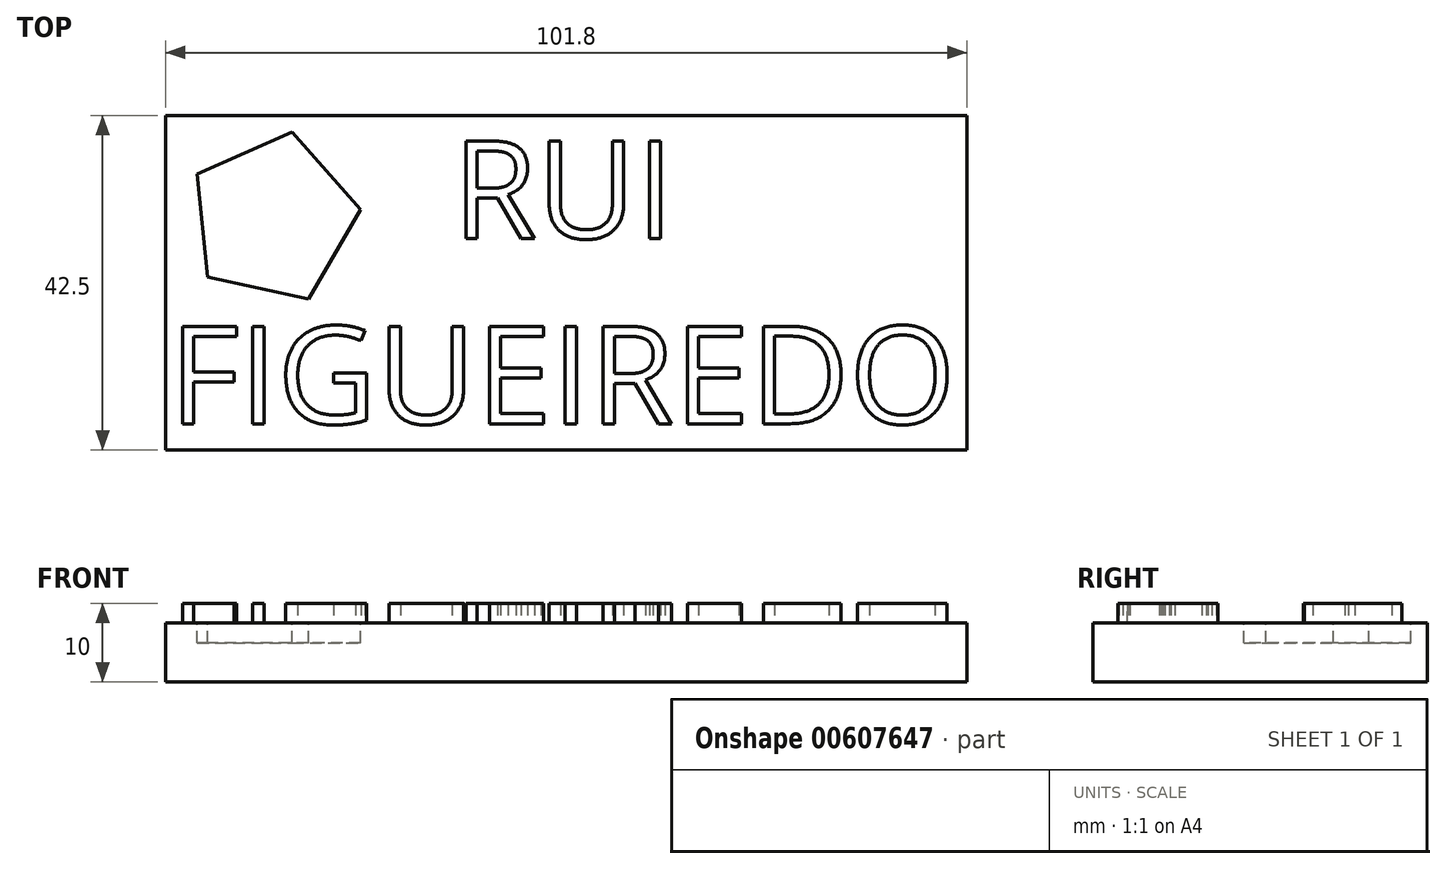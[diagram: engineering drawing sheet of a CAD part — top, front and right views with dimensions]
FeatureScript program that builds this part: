
annotation { "Feature Type Name" : "Feature", "Feature Type Description" : "" }
export const myFeature = defineFeature(function(context is Context, id is Id, definition is map)
    precondition{}
    {
        {
            var Q0;
            Q0=qCreatedBy(makeId("Top.planeOp"),FACE);
            var sketch = newSketch(context, id + "F0", { "sketchPlane" : qUnion([Q0])});
            skLineSegment(sketch, "E0.bottom", {"start": v(-49.13, 21.28) * mm, "end": v(52.67, 21.28) * mm});
            skLineSegment(sketch, "E0.top", {"start": v(-49.13, -21.22) * mm, "end": v(52.67, -21.22) * mm});
            skLineSegment(sketch, "E0.left", {"start": v(-49.13, 21.28) * mm, "end": v(-49.13, -21.22) * mm});
            skLineSegment(sketch, "E0.right", {"start": v(52.67, 21.28) * mm, "end": v(52.67, -21.22) * mm});
            skSolve(sketch);
        }
        {
            var Q0;
            Q0 = qSketchRegion(id + "F0", true);
            extrude(context, id + "F1", {"entities" : qUnion([Q0]), "depth" : 7.5 * mm, "offsetDistance" : 25 * mm});
        }
        {
            var Q0;
            Q0=makeQuery(id+"F1.opExtrude","CAP_FACE",FACE,{"disambiguationData":[OSD([sQuery(id+"F0.wireOp",EDGE,"E0.bottom"),sQuery(id+"F0.wireOp",EDGE,"E0.top"),sQuery(id+"F0.wireOp",EDGE,"E0.left"),sQuery(id+"F0.wireOp",EDGE,"E0.right")])],"isStart":false});
            var sketch = newSketch(context, id + "F2", { "sketchPlane" : qUnion([Q0])});
            skText(sketch, "E1", { "text": "        RUI\nFIGUEIREDO", "fontName": "OpenSans-Regular.ttf"});
            const initialGuessF2  = {"E1": [-0.04868, 0.00566, 1, 0, 0.01247]};
            skSetInitialGuess(sketch, initialGuessF2);
            skSolve(sketch);
        }
        {
            var Q0;
            {var subQ0=sQuery(id+"F0.wireOp",EDGE,"E0.top");var subQ1=sQuery(id+"F0.wireOp",EDGE,"E0.right");var subQ2=sQuery(id+"F0.wireOp",EDGE,"E0.bottom");var subQ3=sQuery(id+"F0.wireOp",EDGE,"E0.left");Q0=makeQuery(id+"FsaKldsH8CgI7bg_1.boolean.opBoolean","SPLIT",FACE,{"disambiguationData":[TD([makeQuery(id+"F1.opExtrude","SWEPT_FACE",FACE,{"disambiguationData":[OSD([subQ2])]})])],"derivedFrom":makeQuery(id+"F1.opExtrude","CAP_FACE",FACE,{"disambiguationData":[OSD([subQ2,subQ0,subQ3,subQ1])],"isStart":false})});}
            var sketch = newSketch(context, id + "F3", { "sketchPlane" : qUnion([Q0])});
            skCircle(sketch, "E2.cCircle", {"center": v(-35.46, 8.21) * mm, "radius": 9.05 * mm, "construction": true});
            skLineSegment(sketch, "E2.0", {"start": v(-24.32, 9.33) * mm, "end": v(-30.95, -2.03) * mm});
            skLineSegment(sketch, "E2.1", {"start": v(-30.95, -2.03) * mm, "end": v(-43.8, 0.76) * mm});
            skLineSegment(sketch, "E2.2", {"start": v(-43.8, 0.76) * mm, "end": v(-45.12, 13.85) * mm});
            skLineSegment(sketch, "E2.3", {"start": v(-45.12, 13.85) * mm, "end": v(-33.08, 19.15) * mm});
            skLineSegment(sketch, "E2.4", {"start": v(-33.08, 19.15) * mm, "end": v(-24.32, 9.33) * mm});
            skPoint(sketch, "E2.0.midPoint", {"position": v(-27.64, 3.65) * mm});
            skSolve(sketch);
        }
        {
            var Q0;
            Q0 = qSketchRegion(id + "F3", true);
            extrude(context, id + "F4", {"entities" : qUnion([Q0]), "operationType" : NewBodyOperationType.REMOVE, "oppositeDirection" : true, "depth" : 2.5 * mm, "offsetDistance" : 25 * mm});
        }
        {
            var Q0;
            Q0 = qSketchRegion(id + "F2", true);
            extrude(context, id + "F5", {"entities" : qUnion([Q0]), "operationType" : NewBodyOperationType.ADD, "depth" : 2.5 * mm, "offsetDistance" : 25 * mm});
        }
    });
